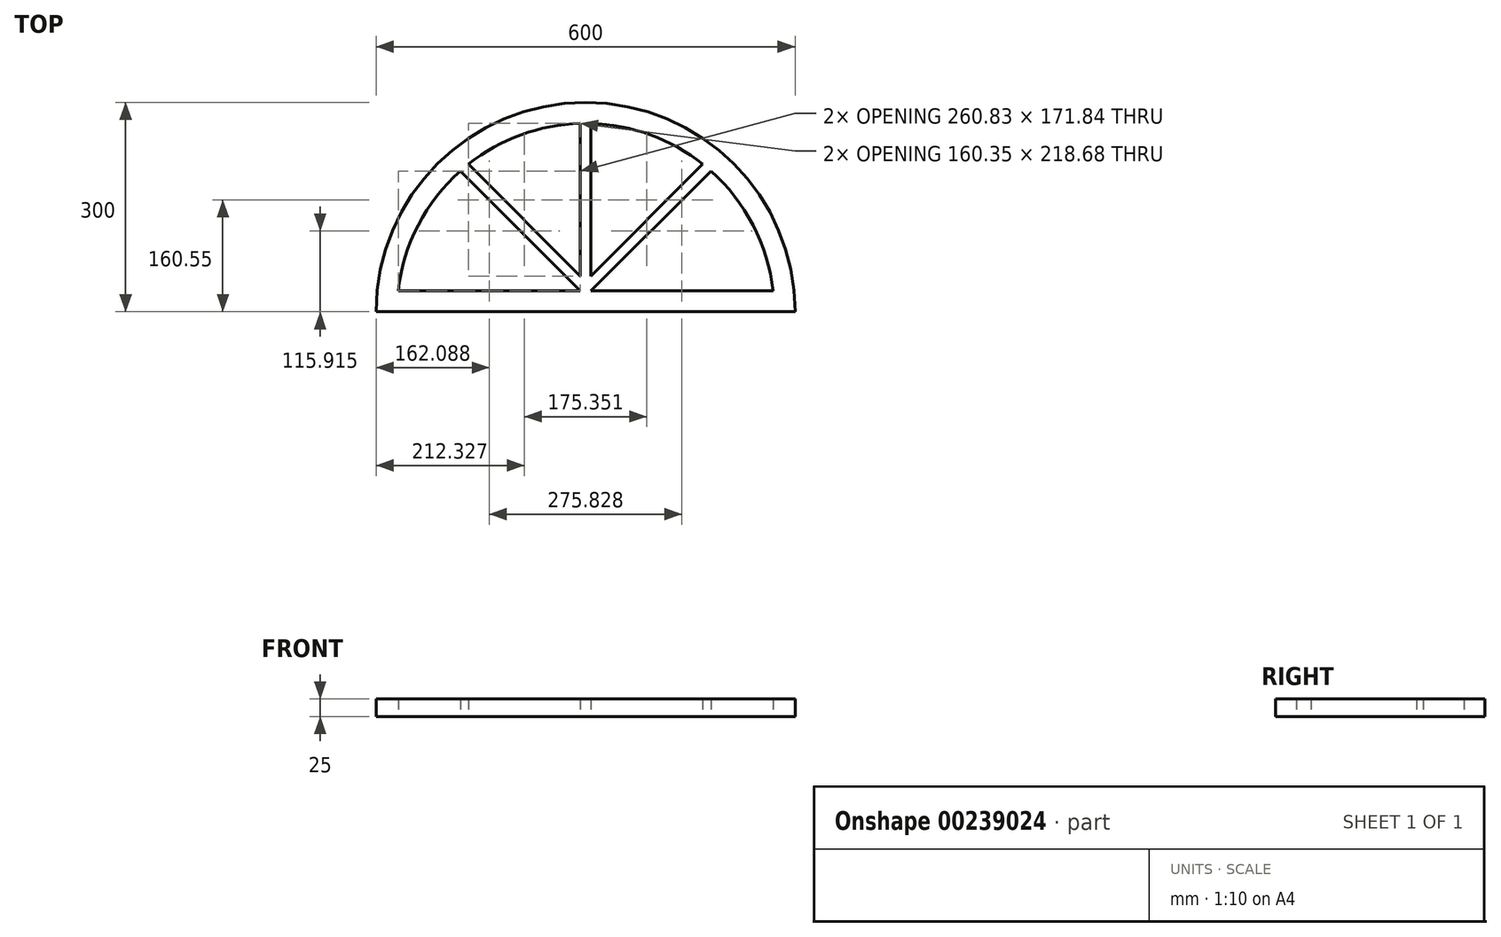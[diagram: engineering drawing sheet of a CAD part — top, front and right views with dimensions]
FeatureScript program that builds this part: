
annotation { "Feature Type Name" : "Feature", "Feature Type Description" : "" }
export const myFeature = defineFeature(function(context is Context, id is Id, definition is map)
    precondition{}
    {
        {
            var Q0;
            Q0=qCreatedBy(makeId("Top.planeOp"),FACE);
            var sketch = newSketch(context, id + "F0", { "sketchPlane" : qUnion([Q0])});
            skLineSegment(sketch, "E0", {"start": v(-317.22, -37.16) * mm, "end": v(282.78, -37.16) * mm});
            skLineSegment(sketch, "E1", {"start": v(-317.22, -37.16) * mm, "end": v(-317.22, -37.16) * mm});
            skLineSegment(sketch, "E2", {"start": v(-17.22, 262.84) * mm, "end": v(-17.22, 262.84) * mm});
            skLineSegment(sketch, "E3", {"start": v(282.78, -37.16) * mm, "end": v(282.78, -37.16) * mm});
            skPoint(sketch, "E4.visualSharp", {"position": v(-317.22, 262.84) * mm});
            skArc(sketch, "E4.filletArc", {"start": v(-17.22, 262.84) * mm, "mid": v(-229.35, 174.97) * mm, "end": v(-317.22, -37.16) * mm});
            skPoint(sketch, "E5.visualSharp", {"position": v(282.78, 262.84) * mm});
            skArc(sketch, "E5.filletArc", {"start": v(282.78, -37.16) * mm, "mid": v(194.91, 174.97) * mm, "end": v(-17.22, 262.84) * mm});
            skLineSegment(sketch, "E6", {"start": v(282.78, -37.16) * mm, "end": v(252.78, -37.16) * mm});
            skArc(sketch, "E7", {"start": v(252.78, -37.16) * mm, "mid": v(-17.22, 232.84) * mm, "end": v(-287.22, -37.16) * mm});
            skLineSegment(sketch, "E8", {"start": v(-9.72, -7.16) * mm, "end": v(251.11, -7.16) * mm});
            skLineSegment(sketch, "E9", {"start": v(-9.72, -7.16) * mm, "end": v(162.12, 164.67) * mm});
            skLineSegment(sketch, "E10", {"start": v(-9.72, 14.05) * mm, "end": v(-9.72, 232.73) * mm});
            skLineSegment(sketch, "E11", {"start": v(150.63, 174.32) * mm, "end": v(-9.72, 14.05) * mm});
            skLineSegment(sketch, "E12", {"start": v(-24.72, -7.16) * mm, "end": v(-285.55, -7.16) * mm});
            skLineSegment(sketch, "E13", {"start": v(-24.72, 14.05) * mm, "end": v(-24.72, 232.73) * mm});
            skLineSegment(sketch, "E14", {"start": v(-24.72, -7.16) * mm, "end": v(-196.55, 164.67) * mm});
            skLineSegment(sketch, "E15", {"start": v(-24.72, 14.05) * mm, "end": v(-185.07, 174.32) * mm});
            skSolve(sketch);
        }
        {
            var Q0;
            {var subQ4=sQuery(id+"F0.wireOp",EDGE,"E4.filletArc");Q0=makeQuery(id+"F0.imprint","IMPRINT",FACE,{"disambiguationData":[TD([[makeQuery(id+"F0.imprint","IMPRINT",EDGE,{"derivedFrom":subQ4}),1.0]])]});}
            var Q1;
            {var subQ11=sQuery(id+"F0.wireOp",EDGE,"E8");Q1=makeQuery(id+"F0.imprint","IMPRINT",FACE,{"disambiguationData":[TD([[makeQuery(id+"F0.imprint","IMPRINT",EDGE,{"derivedFrom":subQ11}),-1.0]])]});}
            extrude(context, id + "F1", {"entities" : qUnion([Q0, Q1]), "depth" : 25 * mm});
        }
    });
